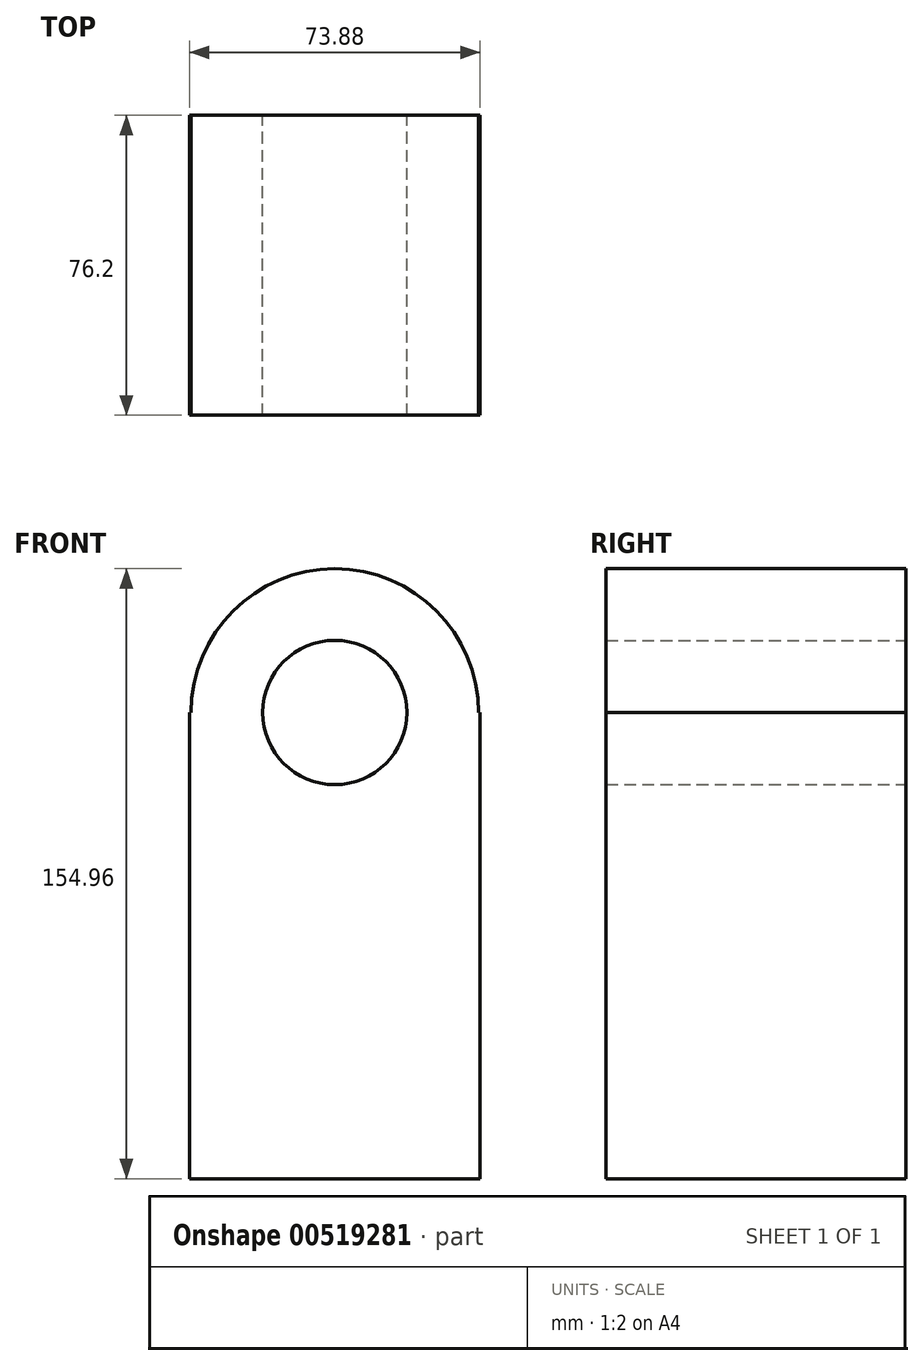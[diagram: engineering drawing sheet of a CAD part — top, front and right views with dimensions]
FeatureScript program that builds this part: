
annotation { "Feature Type Name" : "Feature", "Feature Type Description" : "" }
export const myFeature = defineFeature(function(context is Context, id is Id, definition is map)
    precondition{}
    {
        {
            var Q0;
            Q0=qCreatedBy(makeId("Front.planeOp"),FACE);
            var sketch = newSketch(context, id + "F0", { "sketchPlane" : qUnion([Q0])});
            skLineSegment(sketch, "E0.bottom", {"start": v(36.94, -59.22) * mm, "end": v(-36.94, -59.22) * mm});
            skLineSegment(sketch, "E0.top", {"start": v(36.94, 59.22) * mm, "end": v(36.52, 59.22) * mm});
            skLineSegment(sketch, "E0.left", {"start": v(36.94, -59.22) * mm, "end": v(36.94, 59.22) * mm});
            skLineSegment(sketch, "E0.right", {"start": v(-36.94, -59.22) * mm, "end": v(-36.94, 59.22) * mm});
            skPoint(sketch, "E0.middle", {"position": v(0, 0) * mm});
            skArc(sketch, "E1", {"start": v(36.52, 59.22) * mm, "mid": v(0, 95.74) * mm, "end": v(-36.52, 59.22) * mm});
            skCircle(sketch, "E2", {"center": v(0, 59.22) * mm, "radius": 18.33 * mm});
            skLineSegment(sketch, "E3.trimOffspring", {"start": v(-36.52, 59.22) * mm, "end": v(-36.94, 59.22) * mm});
            skSolve(sketch);
        }
        {
            var Q0;
            Q0=makeQuery(id+"F0.imprint","IMPRINT",FACE,{"disambiguationData":[TD([[makeQuery(id+"F0.imprint","IMPRINT",EDGE,{"derivedFrom":sQuery(id+"F0.wireOp",EDGE,"E0.bottom")}),-1.0]])]});
            extrude(context, id + "F1", {"entities" : qUnion([Q0]), "depth" : 76.2 * mm, "offsetDistance" : 25.4 * mm});
        }
    });
